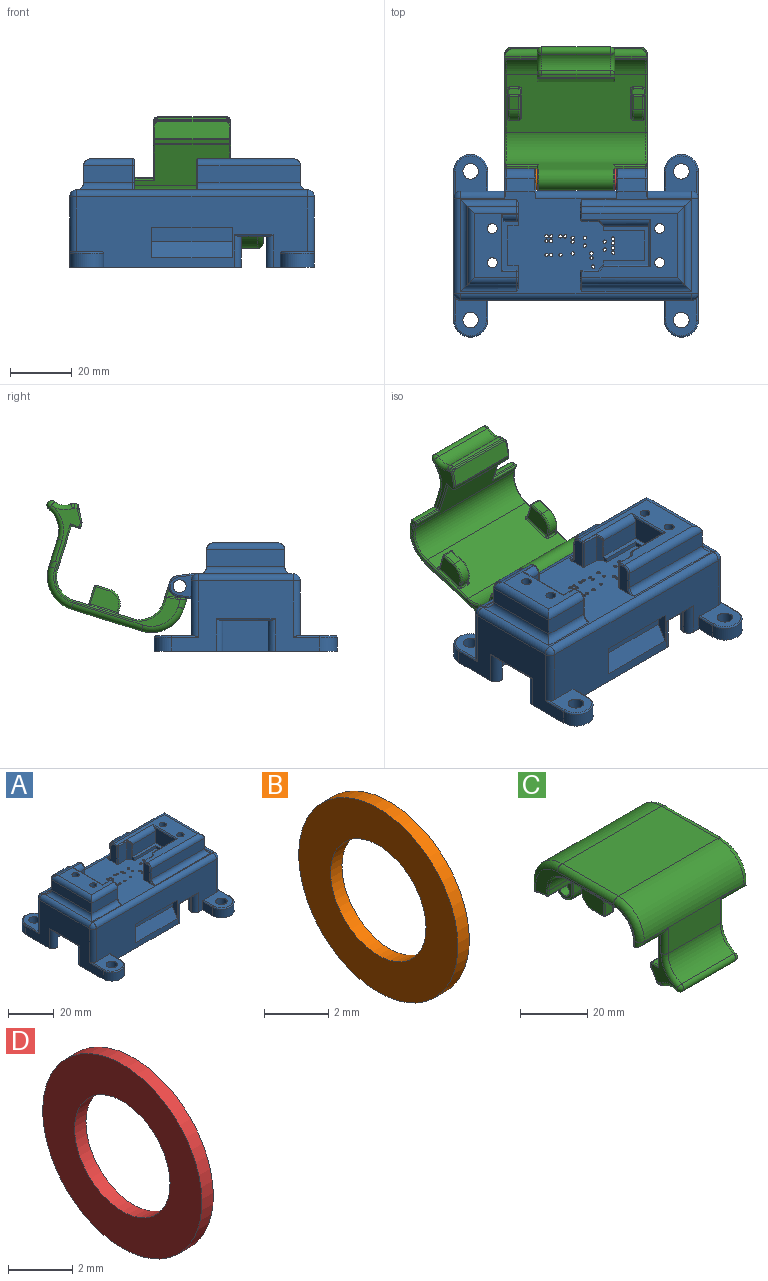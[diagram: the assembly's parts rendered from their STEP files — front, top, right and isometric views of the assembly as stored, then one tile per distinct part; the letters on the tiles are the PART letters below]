
ASSEMBLY  parts=4 mates=3
PART A: 216 faces, bbox 80x60x35.3 mm
  f0: cylinder r=2.25mm len=26.1mm, axis (-1,0,0), area 92mm2, adj f3,f8,f138,f145,f192,f201
  f1: cylinder r=2.25mm len=14.3mm, axis (-1,0,0), area 50.4mm2, adj f3,f8,f103,f139,f198
  f2: plane 74.5x22.75mm, normal (0,-1,0), area 1216.3mm2, adj f19,f21,f89,f91,f94,f96,f100,f107
  f3: plane 74.53x22.78mm, normal (0,1,0), area 1361.4mm2, adj f0,f1,f14,f19,f81,f82,f87,f88
  f4: plane 70x25.24mm, normal (0,0,-1), area 1712.8mm2, adj f12,f13,f17,f18,f41,f42,f43,f44
  f5: plane 14.57x6.25mm, normal (0,-1,0), area 91.1mm2, adj f6,f77,f118,f164
  f6: plane 13.46x8mm, normal (-1,0,0), area 101.4mm2, adj f5,f7,f77,f118,f174
  f7: plane 14.57x8mm, normal (0,1,0), area 116.6mm2, adj f6,f77,f175,f176
  f8: plane 74.63x33.12mm, normal (0,0,1), area 978.8mm2, adj f0,f1,f24,f28,f32,f33,f34,f35
  f9: plane 48x22.75mm, normal (-1,0,0), area 577.5mm2, adj f14,f21,f84,f93,f99,f100,f102,f123
  f10: plane 48x22.75mm, normal (1,0,0), area 777mm2, adj f19,f85,f90,f106,f107,f112,f204,f209
  f11: plane 10x0.5mm, normal (1,0,0), area 5mm2, adj f14,f78,f126,f127
  f12: plane 70x17mm, normal (0,-1,0), area 1058.8mm2, adj f4,f13,f14,f17,f19,f126,f131,f214
  f13: plane 25.24x17mm, normal (1,0,0), area 229.6mm2, adj f4,f12,f14,f18,f21,f123,f128,f211
  f14: plane 55.4x22.25mm, normal (0,0,-1), area 394.9mm2, adj f3,f9,f11,f12,f13,f81,f83,f84
  f15: plane 10x0.5mm, normal (-1,0,0), area 5mm2, adj f19,f79,f129,f130
  f16: plane 10x0.5mm, normal (-1,0,0), area 5mm2, adj f19,f78,f131,f132
  f17: plane 25.24x17mm, normal (-1,0,0), area 429.1mm2, adj f4,f12,f18,f19
  f18: plane 70x17mm, normal (0,1,0), area 1058.8mm2, adj f4,f13,f17,f19,f21,f124,f130,f213
  f19: plane 59x15.6mm, normal (0,0,-1), area 461.4mm2, adj f2,f3,f10,f12,f15,f16,f17,f18
  f20: plane 10x0.5mm, normal (1,0,0), area 5mm2, adj f21,f79,f124,f125
  f21: plane 55.4x22.25mm, normal (0,0,-1), area 394.9mm2, adj f2,f9,f13,f18,f20,f93,f95,f96
  f22: plane 25.24x5.5mm, normal (-1,0,0), area 138.8mm2, adj f23,f29,f101,f120
  f23: plane 15.9x5.5mm, normal (0,-1,0), area 87.5mm2, adj f22,f98,f121,f162
  f24: plane 9.5x6.87mm, normal (1,0,0), area 38.3mm2, adj f8,f68,f71,f158,f160,f161,f162,f163
  f25: plane 8x4.5mm, normal (0,1,0), area 36mm2, adj f26,f71,f157,f158
  f26: plane 16.68x8mm, normal (1,0,0), area 127.2mm2, adj f25,f27,f71,f122,f156
  f27: plane 6.25x4.5mm, normal (0,-1,0), area 28.1mm2, adj f26,f71,f122,f155
  f28: plane 9.5x6.87mm, normal (1,0,0), area 37.6mm2, adj f8,f70,f71,f150,f151,f152,f153,f154
  f29: plane 15.9x5.5mm, normal (0,1,0), area 87.5mm2, adj f22,f97,f119,f151
  f30: plane 20.74x13.65mm, normal (0,0,1), area 174.1mm2, adj f66,f67,f119,f120,f121,f122,f153,f156
  f31: plane 33.1x5.5mm, normal (0,1,0), area 182.1mm2, adj f39,f111,f115,f167
  f32: plane 9.5x4.87mm, normal (-1,0,0), area 35.3mm2, adj f8,f165,f167,f169,f170,f172,f173
  f33: plane 9.49x5.25mm, normal (0,-1,0), area 49.9mm2, adj f8,f34,f166,f168,f169
  f34: plane 9.48x1.61mm, normal (-0.71,-0.71,0), area 19mm2, adj f8,f33,f73,f77,f164,f166
  f35: plane 9.5x1.61mm, normal (-0.71,0.71,0), area 20mm2, adj f8,f36,f72,f77,f175,f178
  f36: plane 9.5x5.25mm, normal (0,1,0), area 49.9mm2, adj f8,f35,f179,f180
  f37: plane 9.5x4.87mm, normal (-1,0,0), area 35.3mm2, adj f8,f179,f182,f183,f184,f185
  f38: plane 33.1x5.5mm, normal (0,-1,0), area 182.1mm2, adj f39,f114,f117,f184
  f39: plane 25.24x5.5mm, normal (1,0,0), area 138.8mm2, adj f31,f38,f113,f116
  f40: plane 30.85x20.74mm, normal (0,0,1), area 273.4mm2, adj f64,f65,f115,f116,f117,f118,f172,f174
  f41: cylinder r=0.55mm len=8mm, axis (0,0,1), area 27.6mm2, adj f4,f8
  f42: cylinder r=0.55mm len=8mm, axis (0,0,1), area 27.6mm2, adj f4,f8
  f43: cylinder r=0.55mm len=8mm, axis (0,0,1), area 27.6mm2, adj f4,f8
  f44: cylinder r=0.55mm len=8mm, axis (0,0,1), area 27.6mm2, adj f4,f8
  f45: cylinder r=0.55mm len=8mm, axis (0,0,1), area 27.6mm2, adj f4,f8
  f46: cylinder r=0.55mm len=8mm, axis (0,0,1), area 27.6mm2, adj f4,f8
  f47: cylinder r=0.55mm len=8mm, axis (0,0,1), area 27.6mm2, adj f4,f8
  f48: cylinder r=0.55mm len=8mm, axis (0,0,1), area 27.6mm2, adj f4,f8
  f49: cylinder r=0.55mm len=8mm, axis (0,0,1), area 27.6mm2, adj f4,f8
  f50: cylinder r=0.55mm len=8mm, axis (0,0,1), area 27.6mm2, adj f4,f8
  f51: cylinder r=0.55mm len=8mm, axis (0,0,1), area 27.6mm2, adj f4,f8
  f52: cylinder r=0.55mm len=8mm, axis (0,0,1), area 27.6mm2, adj f4,f8
  f53: cylinder r=0.55mm len=8mm, axis (0,0,1), area 27.6mm2, adj f4,f8
  f54: cylinder r=0.55mm len=8mm, axis (0,0,1), area 27.6mm2, adj f4,f8
  f55: cylinder r=0.55mm len=8mm, axis (0,0,1), area 27.6mm2, adj f4,f8
  f56: cylinder r=0.55mm len=8mm, axis (0,0,1), area 27.6mm2, adj f4,f8
  f57: cylinder r=0.55mm len=8mm, axis (0,0,1), area 27.6mm2, adj f4,f8
  f58: cylinder r=0.55mm len=8mm, axis (0,0,1), area 27.6mm2, adj f4,f8
  f59: cylinder r=0.55mm len=8mm, axis (0,0,1), area 27.6mm2, adj f4,f8
  f60: cylinder r=0.55mm len=8mm, axis (0,0,1), area 27.6mm2, adj f4,f8
  f61: cylinder r=0.55mm len=8mm, axis (0,0,1), area 27.6mm2, adj f4,f8
  f62: cylinder r=0.55mm len=8mm, axis (0,0,1), area 27.6mm2, adj f4,f8
  f63: cylinder r=0.55mm len=8mm, axis (0,0,1), area 27.6mm2, adj f4,f8
  f64: cylinder r=1.6mm len=18mm, axis (0,0,1), area 181mm2, adj f4,f40
  f65: cylinder r=1.6mm len=18mm, axis (0,0,1), area 181mm2, adj f4,f40
  f66: cylinder r=1.6mm len=18mm, axis (0,0,1), area 181mm2, adj f4,f30
  f67: cylinder r=1.6mm len=18mm, axis (0,0,1), area 181mm2, adj f4,f30
  f68: plane 3.5x1.5mm, normal (0,1,0), area 5.2mm2, adj f8,f24,f69,f71
  f69: plane 12.84x1.5mm, normal (1,0,0), area 19.3mm2, adj f8,f68,f70,f71
  f70: plane 3.5x1.5mm, normal (0,-1,0), area 5.2mm2, adj f8,f28,f69,f71
  f71: plane 16.84x5mm, normal (0,0,1), area 34.4mm2, adj f24,f25,f26,f27,f28,f68,f69,f70
  f72: plane 1.5x1.5mm, normal (-1,0,0), area 2.2mm2, adj f8,f35,f76,f77
  f73: plane 1.5x1.5mm, normal (-1,0,0), area 2.2mm2, adj f8,f34,f74,f77
  f74: plane 13.28x1.5mm, normal (0,-1,0), area 19.9mm2, adj f8,f73,f75,f77
  f75: plane 9.62x1.5mm, normal (-1,0,0), area 14.4mm2, adj f8,f74,f76,f77
  f76: plane 13.28x1.5mm, normal (0,1,0), area 19.9mm2, adj f8,f72,f75,f77
  f77: plane 14.92x12.91mm, normal (0,0,1), area 58.8mm2, adj f5,f6,f7,f34,f35,f72,f73,f74
  f78: plane 9.67x4mm, normal (0,0,-1), area 33.8mm2, adj f11,f16,f126,f127,f131,f132,f214,f215
  f79: plane 9.67x4mm, normal (0,0,-1), area 33.8mm2, adj f15,f20,f124,f125,f129,f130,f212,f213
  f80: plane 16.17x3.5mm, normal (0,0,-1), area 52.5mm2, adj f123,f128,f210,f211
  f81: plane 6.38x4.5mm, normal (1,0,0), area 28.7mm2, adj f3,f14,f84,f191
  f82: plane 12.22x10mm, normal (0,0,1), area 83.9mm2, adj f3,f83,f99,f189,f190,f191
  f83: cylinder r=2.5mm len=5mm, axis (0,0,1), area 78.5mm2, adj f14,f82
  f84: cylinder r=5.5mm len=11mm, axis (0,0,1), area 77.8mm2, adj f9,f14,f81,f190
  f85: cylinder r=5.5mm len=11mm, axis (0,0,1), area 77.8mm2, adj f10,f19,f87,f208
  f86: cylinder r=2.5mm len=5mm, axis (0,0,1), area 78.5mm2, adj f19,f88
  f87: plane 6.38x4.5mm, normal (-1,0,0), area 28.7mm2, adj f3,f19,f85,f207
  f88: plane 12.22x10mm, normal (0,0,1), area 83.9mm2, adj f3,f86,f106,f207,f208,f209
  f89: plane 6.38x4.5mm, normal (-1,0,0), area 28.7mm2, adj f2,f19,f90,f206
  f90: cylinder r=5.5mm len=11mm, axis (0,0,1), area 77.8mm2, adj f10,f19,f89,f205
  f91: plane 12.22x10mm, normal (0,0,1), area 83.9mm2, adj f2,f92,f107,f204,f205,f206
  f92: cylinder r=2.5mm len=5mm, axis (0,0,1), area 78.5mm2, adj f19,f91
  f93: cylinder r=5.5mm len=11mm, axis (0,0,1), area 77.8mm2, adj f9,f21,f96,f187
  f94: plane 12.22x10mm, normal (0,0,1), area 83.9mm2, adj f2,f95,f100,f186,f187,f188
  f95: cylinder r=2.5mm len=5mm, axis (0,0,1), area 78.5mm2, adj f21,f94
  f96: plane 6.38x4.5mm, normal (1,0,0), area 28.7mm2, adj f2,f21,f93,f188
  f97: cylinder r=2.25mm len=18.15mm, axis (-1,0,0), area 60.2mm2, adj f8,f29,f101,f150
  f98: cylinder r=2.25mm len=18.15mm, axis (1,0,0), area 60.2mm2, adj f8,f23,f101,f163
  f99: cylinder r=2.25mm len=18.25mm, axis (0,0,-1), area 63.1mm2, adj f3,f9,f82,f103,f189
  f100: cylinder r=2.25mm len=18.25mm, axis (0,0,1), area 63.1mm2, adj f2,f9,f94,f104,f186
  f101: cylinder r=2.25mm len=29.74mm, axis (0,-1,0), area 97.2mm2, adj f22,f97,f98,f102
  f102: cylinder r=2.25mm len=30.74mm, axis (0,-1,0), area 108.6mm2, adj f8,f9,f101,f103,f104
  f103: sphere r=2.25mm, area 10.8mm2, adj f1,f99,f102
  f104: sphere r=2.25mm, area 8mm2, adj f100,f102,f108
  f105: cylinder r=2.25mm len=14.3mm, axis (-1,0,0), area 50.4mm2, adj f3,f8,f109,f144,f195
  f106: cylinder r=2.25mm len=18.25mm, axis (0,0,1), area 63.1mm2, adj f3,f10,f88,f109,f209
  f107: cylinder r=2.25mm len=18.25mm, axis (0,0,-1), area 63.1mm2, adj f2,f10,f91,f110,f204
  f108: cylinder r=2.25mm len=74.5mm, axis (1,0,0), area 263.3mm2, adj f2,f8,f104,f110
  f109: sphere r=2.25mm, area 5.1mm2, adj f105,f106,f112
  f110: sphere r=2.25mm, area 8mm2, adj f107,f108,f112
  f111: cylinder r=2.25mm len=35.35mm, axis (-1,0,0), area 121mm2, adj f8,f31,f113,f165
  f112: cylinder r=2.25mm len=30.74mm, axis (0,1,0), area 108.6mm2, adj f8,f10,f109,f110,f113
  f113: cylinder r=2.25mm len=29.74mm, axis (0,1,0), area 97.2mm2, adj f39,f111,f112,f114
  f114: cylinder r=2.25mm len=35.35mm, axis (1,0,0), area 121mm2, adj f8,f38,f113,f185
  f115: cylinder r=2.25mm len=33.1mm, axis (1,0,0), area 113mm2, adj f31,f40,f116,f170
  f116: cylinder r=2.25mm len=25.24mm, axis (0,-1,0), area 81.3mm2, adj f39,f40,f115,f117
  f117: cylinder r=2.25mm len=33.1mm, axis (-1,0,0), area 113mm2, adj f38,f40,f116,f183
  f118: cylinder r=2.25mm len=22.14mm, axis (1,0,0), area 55.1mm2, adj f5,f6,f40,f166,f168,f173,f174
  f119: cylinder r=2.25mm len=15.9mm, axis (1,0,0), area 52.2mm2, adj f29,f30,f120,f152
  f120: cylinder r=2.25mm len=25.24mm, axis (0,1,0), area 81.3mm2, adj f22,f30,f119,f121
  f121: cylinder r=2.25mm len=15.9mm, axis (-1,0,0), area 52.2mm2, adj f23,f30,f120,f161
  f122: cylinder r=2.25mm len=5mm, axis (-1,0,0), area 16.3mm2, adj f26,f27,f30,f154,f156
  f123: cylinder r=2.25mm len=10.5mm, axis (0,0,-1), area 71.5mm2, adj f9,f13,f21,f80,f210,f211
  f124: cylinder r=2.25mm len=10.5mm, axis (0,0,1), area 35.7mm2, adj f18,f20,f21,f79,f213
  f125: cylinder r=2.25mm len=10.5mm, axis (0,0,-1), area 35.7mm2, adj f2,f20,f21,f79,f212
  f126: cylinder r=2.25mm len=10.5mm, axis (0,0,-1), area 35.7mm2, adj f11,f12,f14,f78,f214
  f127: cylinder r=2.25mm len=10.5mm, axis (0,0,1), area 35.7mm2, adj f3,f11,f14,f78,f215
  f128: cylinder r=2.25mm len=10.5mm, axis (0,0,1), area 71.5mm2, adj f9,f13,f14,f80,f210,f211
  f129: cylinder r=2.25mm len=10.5mm, axis (0,0,1), area 35.7mm2, adj f2,f15,f19,f79,f212
  f130: cylinder r=2.25mm len=10.5mm, axis (0,0,-1), area 35.7mm2, adj f15,f18,f19,f79,f213
  f131: cylinder r=2.25mm len=10.5mm, axis (0,0,1), area 35.7mm2, adj f12,f16,f19,f78,f214
  f132: cylinder r=2.25mm len=10.5mm, axis (0,0,-1), area 35.7mm2, adj f3,f16,f19,f78,f215
  f133: plane 26x5.2mm, normal (0,-0.87,0.5), area 156mm2, adj f2,f134,f136,f137
  f134: plane 26x4.8mm, normal (0,-1,0), area 124.8mm2, adj f133,f135,f136,f137
  f135: plane 26x3mm, normal (0,0,-1), area 78mm2, adj f2,f134,f136,f137
  f136: plane 10x3mm, normal (-1,0,0), area 22.2mm2, adj f2,f133,f134,f135
  f137: plane 10x3mm, normal (1,0,0), area 22.2mm2, adj f2,f133,f134,f135
  f138: plane 7.71x7.12mm, normal (1,0,0), area 24.9mm2, adj f0,f3,f143,f201,f202,f203
  f139: plane 7.71x7.12mm, normal (-1,0,0), area 24.9mm2, adj f1,f3,f143,f198,f199,f200
  f140: plane 9x4.14mm, normal (0,0.13,-0.99), area 37.6mm2, adj f3,f141,f200,f203
  f141: cylinder r=3.5mm len=9mm, axis (-1,0,0), area 91mm2, adj f140,f142,f199,f202
  f142: plane 9x4.14mm, normal (0,0.13,0.99), area 37.6mm2, adj f8,f141,f198,f201
  f143: cylinder r=2.1mm len=10mm, axis (-1,0,0), area 131.9mm2, adj f138,f139
  f144: plane 7.71x7.12mm, normal (1,0,0), area 24.9mm2, adj f3,f105,f149,f195,f196,f197
  f145: plane 7.71x7.12mm, normal (-1,0,0), area 24.9mm2, adj f0,f3,f149,f192,f193,f194
  f146: plane 9x4.14mm, normal (0,0.13,-0.99), area 37.6mm2, adj f3,f147,f194,f197
  f147: cylinder r=3.5mm len=9mm, axis (-1,0,0), area 91mm2, adj f146,f148,f193,f196
  f148: plane 9x4.14mm, normal (0,0.13,0.99), area 37.6mm2, adj f8,f147,f192,f195
  f149: cylinder r=2.1mm len=10mm, axis (-1,0,0), area 131.9mm2, adj f144,f145
  f150: torus R=2.75mm, axis (-1,0,0), area 2.4mm2, adj f8,f28,f97,f151
  f151: cylinder r=0.5mm len=5.5mm, axis (0,0,1), area 4.3mm2, adj f28,f29,f150,f152
  f152: torus R=1.75mm, axis (-1,0,0), area 2.6mm2, adj f28,f119,f151,f153
  f153: cylinder r=0.5mm len=0.5mm, axis (0,-1,0), area 0.2mm2, adj f28,f30,f152,f154
  f154: torus R=1.75mm, axis (-1,0,0), area 2.6mm2, adj f28,f122,f153,f155
  f155: cylinder r=0.5mm len=6.25mm, axis (0,0,-1), area 4.9mm2, adj f27,f28,f71,f154
  f156: cylinder r=0.5mm len=18.59mm, axis (0,-1,0), area 13.8mm2, adj f26,f30,f122,f157
  f157: cylinder r=0.5mm len=5mm, axis (1,0,0), area 3.7mm2, adj f25,f30,f156,f159
  f158: cylinder r=0.5mm len=8mm, axis (0,0,-1), area 6.3mm2, adj f24,f25,f71,f159
  f159: sphere r=0.5mm, area 0.2mm2, adj f157,f158,f160
  f160: cylinder r=0.5mm len=1.95mm, axis (0,-1,0), area 1.5mm2, adj f24,f30,f159,f161
  f161: torus R=1.75mm, axis (1,0,0), area 2.6mm2, adj f24,f121,f160,f162
  f162: cylinder r=0.5mm len=5.5mm, axis (0,0,1), area 4.3mm2, adj f23,f24,f161,f163
  f163: torus R=2.75mm, axis (1,0,0), area 2.4mm2, adj f8,f24,f98,f162
  f164: cylinder r=0.5mm len=6.25mm, axis (0,0,1), area 2.5mm2, adj f5,f34,f77,f166
  f165: torus R=2.75mm, axis (-1,0,0), area 2.4mm2, adj f8,f32,f111,f167
  f166: bspline ~2.24x2.07mm, area 1.8mm2, adj f33,f34,f118,f164,f168
  f167: cylinder r=0.5mm len=5.5mm, axis (0,0,-1), area 4.3mm2, adj f31,f32,f165,f170
  f168: cylinder r=0.5mm len=5.46mm, axis (1,0,0), area 4mm2, adj f33,f118,f166,f171
  f169: cylinder r=0.5mm len=9.49mm, axis (0,0,1), area 7.5mm2, adj f8,f32,f33,f171
  f170: torus R=1.75mm, axis (-1,0,0), area 2.6mm2, adj f32,f115,f167,f172
  f171: sphere r=0.5mm, area 0.2mm2, adj f168,f169,f173
  f172: cylinder r=0.5mm len=1.81mm, axis (0,1,0), area 1.4mm2, adj f32,f40,f170,f173
  f173: torus R=1.75mm, axis (-1,0,0), area 0.1mm2, adj f32,f118,f171,f172
  f174: cylinder r=0.5mm len=15.37mm, axis (0,-1,0), area 11.3mm2, adj f6,f40,f118,f176
  f175: cylinder r=0.5mm len=8mm, axis (0,0,1), area 3.1mm2, adj f7,f35,f77,f177
  f176: cylinder r=0.5mm len=15.07mm, axis (-1,0,0), area 11.6mm2, adj f7,f40,f174,f177
  f177: sphere r=0.5mm, area 0.1mm2, adj f175,f176,f178
  f178: cylinder r=0.5mm len=1.96mm, axis (0.71,0.71,0), area 1.7mm2, adj f35,f40,f177,f180
  f179: cylinder r=0.5mm len=9.5mm, axis (0,0,1), area 7.5mm2, adj f8,f36,f37,f181
  f180: cylinder r=0.5mm len=5.46mm, axis (1,0,0), area 4.2mm2, adj f36,f40,f178,f181
  f181: sphere r=0.5mm, area 0.5mm2, adj f179,f180,f182
  f182: cylinder r=0.5mm len=1.95mm, axis (0,1,0), area 1.5mm2, adj f37,f40,f181,f183
  f183: torus R=1.75mm, axis (1,0,0), area 2.6mm2, adj f37,f117,f182,f184
  f184: cylinder r=0.5mm len=5.5mm, axis (0,0,-1), area 4.3mm2, adj f37,f38,f183,f185
  f185: torus R=2.75mm, axis (1,0,0), area 2.4mm2, adj f8,f37,f114,f184
  f186: cylinder r=0.5mm len=8.63mm, axis (0,1,0), area 6.2mm2, adj f9,f94,f100,f187
  f187: torus R=5mm, axis (0,0,1), area 13.1mm2, adj f93,f94,f186,f188
  f188: cylinder r=0.5mm len=6.38mm, axis (0,1,0), area 5mm2, adj f2,f94,f96,f187
  f189: cylinder r=0.5mm len=8.63mm, axis (0,1,0), area 6.2mm2, adj f9,f82,f99,f190
  f190: torus R=5mm, axis (0,0,1), area 13.1mm2, adj f82,f84,f189,f191
  f191: cylinder r=0.5mm len=6.38mm, axis (0,1,0), area 5mm2, adj f3,f81,f82,f190
  f192: cylinder r=0.5mm len=6.42mm, axis (0,-0.99,0.13), area 4mm2, adj f0,f8,f145,f148,f193
  f193: torus R=3mm, axis (1,0,0), area 7.5mm2, adj f145,f147,f192,f194
  f194: cylinder r=0.5mm len=4.21mm, axis (0,0.99,0.13), area 3.3mm2, adj f3,f145,f146,f193
  f195: cylinder r=0.5mm len=6.42mm, axis (0,0.99,-0.13), area 4mm2, adj f8,f105,f144,f148,f196
  f196: torus R=3mm, axis (1,0,0), area 7.5mm2, adj f144,f147,f195,f197
  f197: cylinder r=0.5mm len=4.21mm, axis (0,-0.99,-0.13), area 3.3mm2, adj f3,f144,f146,f196
  f198: cylinder r=0.5mm len=6.42mm, axis (0,-0.99,0.13), area 4mm2, adj f1,f8,f139,f142,f199
  f199: torus R=3mm, axis (1,0,0), area 7.5mm2, adj f139,f141,f198,f200
  f200: cylinder r=0.5mm len=4.21mm, axis (0,0.99,0.13), area 3.3mm2, adj f3,f139,f140,f199
  f201: cylinder r=0.5mm len=6.42mm, axis (0,0.99,-0.13), area 4mm2, adj f0,f8,f138,f142,f202
  f202: torus R=3mm, axis (1,0,0), area 7.5mm2, adj f138,f141,f201,f203
  f203: cylinder r=0.5mm len=4.21mm, axis (0,-0.99,-0.13), area 3.3mm2, adj f3,f138,f140,f202
  f204: cylinder r=0.5mm len=8.63mm, axis (0,-1,0), area 6.2mm2, adj f10,f91,f107,f205
  f205: torus R=5mm, axis (0,0,1), area 13.1mm2, adj f90,f91,f204,f206
  f206: cylinder r=0.5mm len=6.38mm, axis (0,-1,0), area 5mm2, adj f2,f89,f91,f205
  f207: cylinder r=0.5mm len=6.38mm, axis (0,-1,0), area 5mm2, adj f3,f87,f88,f208
  f208: torus R=5mm, axis (0,0,1), area 13.1mm2, adj f85,f88,f207,f209
  f209: cylinder r=0.5mm len=8.63mm, axis (0,-1,0), area 6.2mm2, adj f10,f88,f106,f208
  f210: cylinder r=0.5mm len=19mm, axis (0,1,0), area 13.8mm2, adj f9,f80,f123,f128
  f211: cylinder r=0.5mm len=19mm, axis (0,-1,0), area 13.8mm2, adj f13,f80,f123,f128
  f212: cylinder r=0.5mm len=12.5mm, axis (-1,0,0), area 8.7mm2, adj f2,f79,f125,f129
  f213: cylinder r=0.5mm len=12.5mm, axis (1,0,0), area 8.7mm2, adj f18,f79,f124,f130
  f214: cylinder r=0.5mm len=12.5mm, axis (-1,0,0), area 8.7mm2, adj f12,f78,f126,f131
  f215: cylinder r=0.5mm len=12.5mm, axis (1,0,0), area 8.7mm2, adj f3,f78,f127,f132
PART B: 4 faces, bbox 0.5x7x7 mm
  f0: cylinder r=2.1mm len=4.2mm, axis (-1,0,0), area 6.6mm2, adj f2,f3
  f1: cylinder r=3.5mm len=7mm, axis (-1,0,0), area 11mm2, adj f2,f3
  f2: plane 7x7mm, normal (1,0,0), area 24.6mm2, adj f0,f1
  f3: plane 7x7mm, normal (-1,0,0), area 24.6mm2, adj f0,f1
PART C: 153 faces, bbox 46x53.1x33.8 mm
  f0: plane 10x3.54mm, normal (0,-0.13,-0.99), area 35.7mm2, adj f1,f31,f80,f86,f87
  f1: cylinder r=3.8mm len=10mm, axis (-1,0,0), area 24mm2, adj f0,f31,f71,f78,f81
  f2: plane 10.5x0.5mm, normal (0,0,-1), area 5.3mm2, adj f17,f27,f56,f102
  f3: plane 45x19.64mm, normal (0,0,-1), area 775.5mm2, adj f4,f15,f79,f82,f85,f88,f91,f93
  f4: cylinder r=8mm len=45mm, axis (-1,0,0), area 565.5mm2, adj f3,f5,f97,f136
  f5: plane 45x6.5mm, normal (0,-1,0), area 193.4mm2, adj f4,f29,f80,f86,f95,f123,f126,f134
  f6: plane 10x3.54mm, normal (0,-0.13,-0.99), area 35.7mm2, adj f7,f30,f123,f125,f126
  f7: cylinder r=3.8mm len=10mm, axis (-1,0,0), area 24mm2, adj f6,f30,f116,f119,f122
  f8: plane 42x6.5mm, normal (0,1,0), area 217.5mm2, adj f9,f29,f61,f67,f68,f71,f116,f117
  f9: cylinder r=11mm len=42mm, axis (-1,0,0), area 725.7mm2, adj f8,f10,f60,f66
  f10: plane 42x23.64mm, normal (0,0,1), area 992.9mm2, adj f9,f11,f59,f65
  f11: cylinder r=11mm len=42mm, axis (-1,0,0), area 725.7mm2, adj f10,f12,f58,f64
  f12: plane 42x9.38mm, normal (0,-1,0), area 210.5mm2, adj f11,f24,f44,f50,f56,f57,f62,f63
  f13: plane 10.5x0.5mm, normal (0,0,-1), area 5.3mm2, adj f16,f26,f62,f127
  f14: plane 45x14.7mm, normal (0,1,0), area 388.5mm2, adj f15,f23,f100,f102,f105,f124,f127,f130
  f15: cylinder r=8mm len=45mm, axis (-1,0,0), area 565.5mm2, adj f3,f14,f99,f135
  f16: plane 41.64x11.47mm, normal (1,0,0), area 70mm2, adj f13,f63,f64,f65,f66,f67,f122,f125
  f17: plane 41.64x11.47mm, normal (-1,0,0), area 70mm2, adj f2,f57,f58,f59,f60,f61,f81,f87
  f18: cylinder r=5mm len=22mm, axis (-1,0,0), area 121.7mm2, adj f19,f25,f47,f53
  f19: cylinder r=2mm len=22mm, axis (-1,0,0), area 31.8mm2, adj f18,f20,f48,f54
  f20: plane 22x0.71mm, normal (0,0,-1), area 15.6mm2, adj f19,f49,f55,f104
  f21: plane 24x4.83mm, normal (0,0.87,-0.5), area 133.4mm2, adj f101,f103,f104,f107,f110,f111
  f22: plane 24x1.37mm, normal (0,1,0), area 32.8mm2, adj f109,f110,f114,f115
  f23: plane 24x2.5mm, normal (0,0,1), area 60mm2, adj f14,f108,f114,f121
  f24: cylinder r=9mm len=22mm, axis (-1,0,0), area 235mm2, adj f12,f25,f45,f51
  f25: cylinder r=1.5mm len=22mm, axis (-1,0,0), area 103.7mm2, adj f18,f24,f46,f52
  f26: plane 18.26x10.57mm, normal (1,0,0), area 46.4mm2, adj f13,f50,f51,f53,f54,f55,f62,f111
  f27: plane 18.26x10.57mm, normal (-1,0,0), area 46.4mm2, adj f2,f44,f45,f47,f48,f49,f56,f103
  f28: cylinder r=2.1mm len=25mm, axis (-1,0,0), area 329.9mm2, adj f30,f31
  f29: cylinder r=3.5mm len=24mm, axis (-1,0,0), area 263.9mm2, adj f5,f8,f72,f120
  f30: plane 7.21x6mm, normal (1,0,0), area 22.5mm2, adj f6,f7,f28,f116,f117,f120,f123
  f31: plane 7.21x6mm, normal (-1,0,0), area 22.5mm2, adj f0,f1,f28,f68,f71,f72,f80
  f32: plane 5.8x3mm, normal (0,-1,0), area 17.4mm2, adj f74,f75,f88,f89
  f33: plane 4.5x3mm, normal (0,0,-1), area 13.5mm2, adj f34,f69,f75,f76
  f34: cylinder r=5mm len=5mm, axis (-1,0,0), area 23.6mm2, adj f33,f35,f73,f84
  f35: plane 3x1.3mm, normal (0,1,0), area 3.9mm2, adj f34,f77,f90,f91
  f36: plane 9x5.8mm, normal (1,0,0), area 47.9mm2, adj f69,f73,f74,f77,f79
  f37: plane 9x5.8mm, normal (-1,0,0), area 47.9mm2, adj f76,f84,f89,f90,f96
  f38: plane 5.8x3mm, normal (0,-1,0), area 17.4mm2, adj f128,f137,f138,f139
  f39: plane 4.5x3mm, normal (0,0,-1), area 13.5mm2, adj f40,f128,f133,f140
  f40: cylinder r=5mm len=5mm, axis (-1,0,0), area 23.6mm2, adj f39,f41,f141,f145
  f41: plane 3x1.3mm, normal (0,1,0), area 3.9mm2, adj f40,f146,f149,f152
  f42: plane 9x5.8mm, normal (1,0,0), area 47.9mm2, adj f133,f137,f141,f146,f147
  f43: plane 9x5.8mm, normal (-1,0,0), area 47.9mm2, adj f139,f140,f145,f148,f149
  f44: cylinder r=1.5mm len=9.18mm, axis (0,0,-1), area 18.9mm2, adj f12,f27,f45,f56
  f45: torus R=10.5mm, axis (1,0,0), area 26.7mm2, adj f24,f27,f44,f46
  f46: sphere r=1.5mm, area 7.1mm2, adj f25,f45,f47
  f47: torus R=6.5mm, axis (1,0,0), area 14.5mm2, adj f18,f27,f46,f48
  f48: torus R=0.5mm, axis (1,0,0), area 2.5mm2, adj f19,f27,f47,f49
  f49: cylinder r=1.5mm len=1.5mm, axis (0,1,0), area 2.2mm2, adj f20,f27,f48,f101
  f50: cylinder r=1.5mm len=9.18mm, axis (0,0,1), area 18.9mm2, adj f12,f26,f51,f62
  f51: torus R=10.5mm, axis (1,0,0), area 26.7mm2, adj f24,f26,f50,f52
  f52: sphere r=1.5mm, area 7.1mm2, adj f25,f51,f53
  f53: torus R=6.5mm, axis (1,0,0), area 14.5mm2, adj f18,f26,f52,f54
  f54: torus R=0.5mm, axis (1,0,0), area 2.5mm2, adj f19,f26,f53,f55
  f55: cylinder r=1.5mm len=1.5mm, axis (0,-1,0), area 2.2mm2, adj f20,f26,f54,f107
  f56: cylinder r=2mm len=12mm, axis (-1,0,0), area 32.2mm2, adj f2,f12,f27,f44,f57
  f57: cylinder r=2mm len=2.2mm, axis (0,0,-1), area 4.6mm2, adj f12,f17,f56,f58
  f58: torus R=9mm, axis (1,0,0), area 50.7mm2, adj f11,f17,f57,f59
  f59: cylinder r=2mm len=23.64mm, axis (0,-1,0), area 74.3mm2, adj f10,f17,f58,f60
  f60: torus R=9mm, axis (1,0,0), area 50.7mm2, adj f9,f17,f59,f61
  f61: cylinder r=2mm len=3.42mm, axis (0,0,1), area 9.5mm2, adj f8,f17,f60,f78
  f62: cylinder r=2mm len=12mm, axis (-1,0,0), area 32.2mm2, adj f12,f13,f26,f50,f63
  f63: cylinder r=2mm len=2.2mm, axis (0,0,1), area 4.6mm2, adj f12,f16,f62,f64
  f64: torus R=9mm, axis (1,0,0), area 50.7mm2, adj f11,f16,f63,f65
  f65: cylinder r=2mm len=23.64mm, axis (0,1,0), area 74.3mm2, adj f10,f16,f64,f66
  f66: torus R=9mm, axis (1,0,0), area 50.7mm2, adj f9,f16,f65,f67
  f67: cylinder r=2mm len=3.42mm, axis (0,0,-1), area 9.5mm2, adj f8,f16,f66,f119
  f68: cylinder r=0.5mm len=3.08mm, axis (0,0,1), area 2.2mm2, adj f8,f31,f71,f72
  f69: cylinder r=0.5mm len=4.5mm, axis (0,-1,0), area 3.5mm2, adj f33,f36,f70,f73
  f70: sphere r=0.5mm, area 0.4mm2, adj f69,f74,f75
  f71: cylinder r=0.5mm len=9mm, axis (-1,0,0), area 10.1mm2, adj f1,f8,f31,f68,f78
  f72: torus R=3mm, axis (1,0,0), area 8.2mm2, adj f29,f31,f68,f80
  f73: torus R=4.5mm, axis (1,0,0), area 5.9mm2, adj f34,f36,f69,f77
  f74: cylinder r=0.5mm len=5.8mm, axis (0,0,1), area 4.6mm2, adj f32,f36,f70,f82
  f75: cylinder r=0.5mm len=3mm, axis (1,0,0), area 2.4mm2, adj f32,f33,f70,f83
  f76: cylinder r=0.5mm len=4.5mm, axis (0,1,0), area 3.5mm2, adj f33,f37,f83,f84
  f77: cylinder r=0.5mm len=1.3mm, axis (0,0,-1), area 1mm2, adj f35,f36,f73,f85
  f78: bspline ~2.58x2.55mm, area 3mm2, adj f1,f61,f71,f81
  f79: cylinder r=0.5mm len=9mm, axis (0,1,0), area 7.1mm2, adj f3,f36,f82,f85
  f80: cylinder r=0.5mm len=4.72mm, axis (0,0,-1), area 3.5mm2, adj f0,f5,f31,f72,f86
  f81: torus R=4.3mm, axis (1,0,0), area 0.7mm2, adj f1,f17,f78,f87
  f82: torus R=1mm, axis (0,0,1), area 0.8mm2, adj f3,f74,f79,f88
  f83: sphere r=0.5mm, area 0.4mm2, adj f75,f76,f89
  f84: torus R=4.5mm, axis (1,0,0), area 5.9mm2, adj f34,f37,f76,f90
  f85: torus R=1mm, axis (0,0,1), area 0.8mm2, adj f3,f77,f79,f91
  f86: cylinder r=0.5mm len=10.5mm, axis (-1,0,0), area 7.4mm2, adj f0,f5,f80,f92
  f87: cylinder r=0.5mm len=3.61mm, axis (0,0.99,-0.13), area 2.8mm2, adj f0,f17,f81,f92
  f88: cylinder r=0.5mm len=3mm, axis (-1,0,0), area 2.4mm2, adj f3,f32,f82,f93
  f89: cylinder r=0.5mm len=5.8mm, axis (0,0,-1), area 4.6mm2, adj f32,f37,f83,f93
  f90: cylinder r=0.5mm len=1.3mm, axis (0,0,1), area 1mm2, adj f35,f37,f84,f94
  f91: cylinder r=0.5mm len=3mm, axis (1,0,0), area 2.4mm2, adj f3,f35,f85,f94
  f92: sphere r=0.5mm, area 0.4mm2, adj f86,f87,f95
  f93: torus R=1mm, axis (0,0,1), area 0.8mm2, adj f3,f88,f89,f96
  f94: torus R=1mm, axis (0,0,1), area 0.8mm2, adj f3,f90,f91,f96
  f95: cylinder r=0.5mm len=1.78mm, axis (0,0,-1), area 1.4mm2, adj f5,f17,f92,f97
  f96: cylinder r=0.5mm len=9mm, axis (0,-1,0), area 7.1mm2, adj f37,f93,f94,f98
  f97: torus R=8.5mm, axis (1,0,0), area 10.1mm2, adj f4,f17,f95,f98
  f98: cylinder r=0.5mm len=19.64mm, axis (0,1,0), area 15.4mm2, adj f3,f17,f96,f97,f99
  f99: torus R=8.5mm, axis (1,0,0), area 10.1mm2, adj f15,f17,f98,f100
  f100: cylinder r=0.5mm len=2.2mm, axis (0,0,1), area 1.6mm2, adj f14,f17,f99,f102
  f101: bspline ~1.5x1.5mm, area 1.3mm2, adj f21,f49,f103,f104
  f102: cylinder r=0.5mm len=11mm, axis (1,0,0), area 8.2mm2, adj f2,f14,f100,f105
  f103: cylinder r=0.5mm len=4.08mm, axis (0,0.5,0.87), area 3.5mm2, adj f21,f27,f101,f106
  f104: cylinder r=0.5mm len=22mm, axis (-1,0,0), area 11.5mm2, adj f20,f21,f101,f107
  f105: cylinder r=0.5mm len=13.5mm, axis (0,0,1), area 10.1mm2, adj f14,f27,f102,f108
  f106: sphere r=0.5mm, area 0.1mm2, adj f103,f109,f110
  f107: bspline ~1.5x1.5mm, area 1.3mm2, adj f21,f55,f104,f111
  f108: cylinder r=0.5mm len=3mm, axis (0,-1,0), area 2.1mm2, adj f23,f27,f105,f112
  f109: cylinder r=0.5mm len=1.37mm, axis (0,0,1), area 1.1mm2, adj f22,f27,f106,f112
  f110: cylinder r=0.5mm len=24mm, axis (-1,0,0), area 6.3mm2, adj f21,f22,f106,f113
  f111: cylinder r=0.5mm len=4.08mm, axis (0,-0.5,-0.87), area 3.5mm2, adj f21,f26,f107,f113
  f112: sphere r=0.5mm, area 0.4mm2, adj f108,f109,f114
  f113: sphere r=0.5mm, area 0.1mm2, adj f110,f111,f115
  f114: cylinder r=0.5mm len=24mm, axis (-1,0,0), area 18.8mm2, adj f22,f23,f112,f118
  f115: cylinder r=0.5mm len=1.37mm, axis (0,0,-1), area 1.1mm2, adj f22,f26,f113,f118
  f116: cylinder r=0.5mm len=9mm, axis (-1,0,0), area 10.1mm2, adj f7,f8,f30,f117,f119
  f117: cylinder r=0.5mm len=3.08mm, axis (0,0,-1), area 2.2mm2, adj f8,f30,f116,f120
  f118: sphere r=0.5mm, area 0.4mm2, adj f114,f115,f121
  f119: bspline ~2.58x2.27mm, area 3mm2, adj f7,f67,f116,f122
  f120: torus R=3mm, axis (1,0,0), area 8.2mm2, adj f29,f30,f117,f123
  f121: cylinder r=0.5mm len=3mm, axis (0,1,0), area 2.1mm2, adj f23,f26,f118,f124
  f122: torus R=4.3mm, axis (1,0,0), area 0.7mm2, adj f7,f16,f119,f125
  f123: cylinder r=0.5mm len=4.72mm, axis (0,0,1), area 3.5mm2, adj f5,f6,f30,f120,f126
  f124: cylinder r=0.5mm len=13.5mm, axis (0,0,-1), area 10.1mm2, adj f14,f26,f121,f127
  f125: cylinder r=0.5mm len=3.61mm, axis (0,-0.99,0.13), area 2.8mm2, adj f6,f16,f122,f129
  f126: cylinder r=0.5mm len=10.5mm, axis (-1,0,0), area 7.4mm2, adj f5,f6,f123,f129
  f127: cylinder r=0.5mm len=11mm, axis (1,0,0), area 8.2mm2, adj f13,f14,f124,f130
  f128: cylinder r=0.5mm len=3mm, axis (1,0,0), area 2.4mm2, adj f38,f39,f131,f132
  f129: sphere r=0.5mm, area 0.4mm2, adj f125,f126,f134
  f130: cylinder r=0.5mm len=2.2mm, axis (0,0,-1), area 1.6mm2, adj f14,f16,f127,f135
  f131: sphere r=0.5mm, area 0.4mm2, adj f128,f133,f137
  f132: sphere r=0.5mm, area 0.4mm2, adj f128,f139,f140
  f133: cylinder r=0.5mm len=4.5mm, axis (0,-1,0), area 3.5mm2, adj f39,f42,f131,f141
  f134: cylinder r=0.5mm len=1.78mm, axis (0,0,1), area 1.4mm2, adj f5,f16,f129,f136
  f135: torus R=8.5mm, axis (1,0,0), area 10.1mm2, adj f15,f16,f130,f143
  f136: torus R=8.5mm, axis (1,0,0), area 10.1mm2, adj f4,f16,f134,f143
  f137: cylinder r=0.5mm len=5.8mm, axis (0,0,1), area 4.6mm2, adj f38,f42,f131,f142
  f138: cylinder r=0.5mm len=3mm, axis (-1,0,0), area 2.4mm2, adj f3,f38,f142,f144
  f139: cylinder r=0.5mm len=5.8mm, axis (0,0,-1), area 4.6mm2, adj f38,f43,f132,f144
  f140: cylinder r=0.5mm len=4.5mm, axis (0,1,0), area 3.5mm2, adj f39,f43,f132,f145
  f141: torus R=4.5mm, axis (1,0,0), area 5.9mm2, adj f40,f42,f133,f146
  f142: torus R=1mm, axis (0,0,1), area 0.8mm2, adj f3,f137,f138,f147
  f143: cylinder r=0.5mm len=19.64mm, axis (0,-1,0), area 15.4mm2, adj f3,f16,f135,f136,f147
  f144: torus R=1mm, axis (0,0,1), area 0.8mm2, adj f3,f138,f139,f148
  f145: torus R=4.5mm, axis (1,0,0), area 5.9mm2, adj f40,f43,f140,f149
  f146: cylinder r=0.5mm len=1.3mm, axis (0,0,-1), area 1mm2, adj f41,f42,f141,f150
  f147: cylinder r=0.5mm len=9mm, axis (0,1,0), area 7.1mm2, adj f42,f142,f143,f150
  f148: cylinder r=0.5mm len=9mm, axis (0,-1,0), area 7.1mm2, adj f3,f43,f144,f151
  f149: cylinder r=0.5mm len=1.3mm, axis (0,0,1), area 1mm2, adj f41,f43,f145,f151
  f150: torus R=1mm, axis (0,0,1), area 0.8mm2, adj f3,f146,f147,f152
  f151: torus R=1mm, axis (0,0,1), area 0.8mm2, adj f3,f148,f149,f152
  f152: cylinder r=0.5mm len=3mm, axis (1,0,0), area 2.4mm2, adj f3,f41,f150,f151
PART D: 4 faces, bbox 0.5x7x7 mm
  f0: cylinder r=2.1mm len=4.2mm, axis (-1,0,0), area 6.6mm2, adj f2,f3
  f1: cylinder r=3.5mm len=7mm, axis (-1,0,0), area 11mm2, adj f2,f3
  f2: plane 7x7mm, normal (1,0,0), area 24.6mm2, adj f0,f1
  f3: plane 7x7mm, normal (-1,0,0), area 24.6mm2, adj f0,f1
PLACE A t=(12,-12.62,25)mm
PLACE B t=(12,-12.62,25)mm
PLACE C rot(axis=(-1,0,0),162.7deg) t=(12,30.24,23.53)mm
PLACE D t=(12,-12.62,25)mm
MATE revolute B.f0 <-> A.f141  axis (-1,0,0) through (22,8.7,21)mm
MATE revolute A.f141 <-> D.f0  axis (-1,0,0) through (48,8.7,21)mm
MATE revolute B.f0 <-> C.f1  axis (1,0,0) through (22.5,8.7,21)mm
